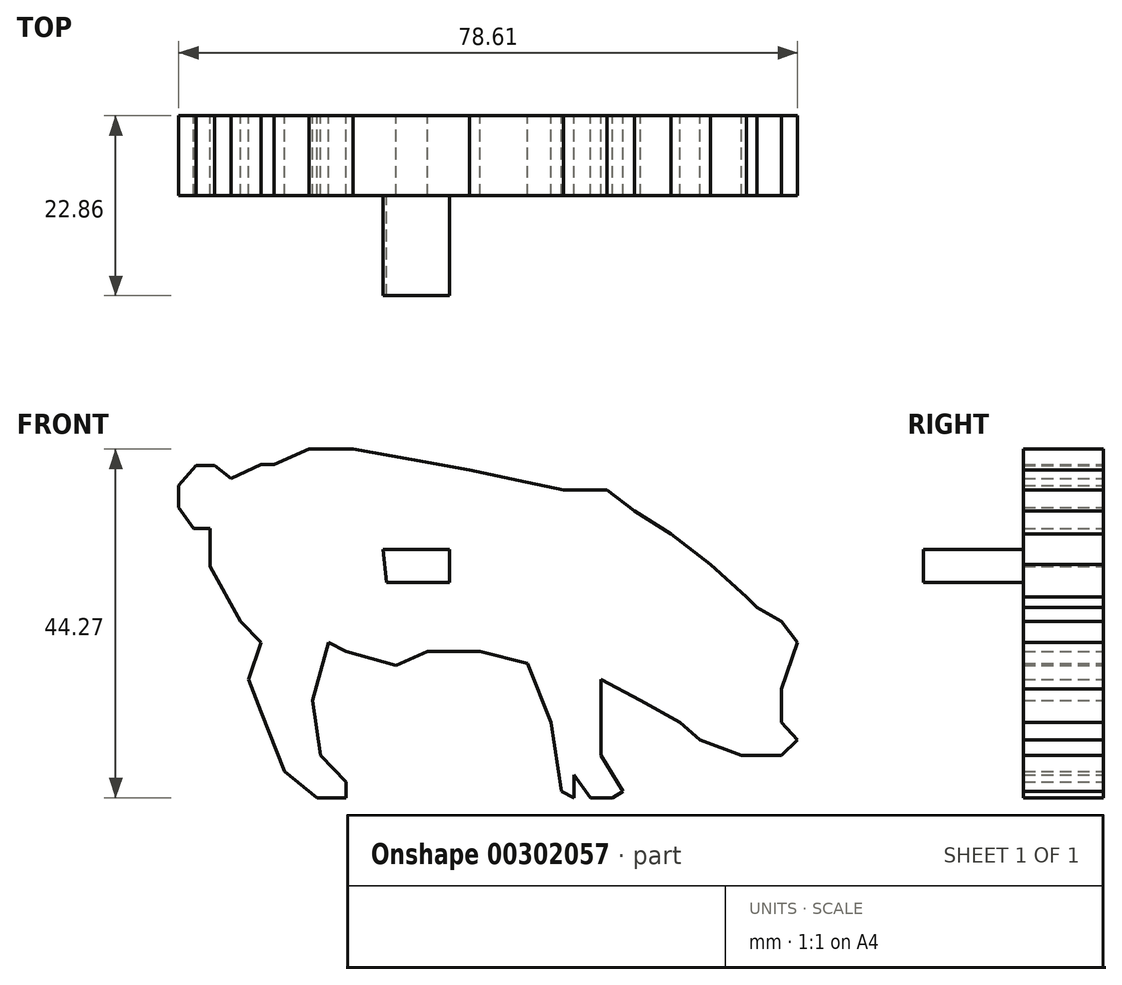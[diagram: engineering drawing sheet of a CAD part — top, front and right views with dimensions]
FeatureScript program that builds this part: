
annotation { "Feature Type Name" : "Feature", "Feature Type Description" : "" }
export const myFeature = defineFeature(function(context is Context, id is Id, definition is map)
    precondition{}
    {
        {
            var Q0;
            Q0=qCreatedBy(makeId("Front.planeOp"),FACE);
            var sketch = newSketch(context, id + "F0", { "sketchPlane" : qUnion([Q0])});
            skLineSegment(sketch, "E0", {"start": v(-64.38, 63.8) * mm, "end": v(-59.95, 65.71) * mm});
            skLineSegment(sketch, "E1", {"start": v(-59.95, 65.71) * mm, "end": v(-54.34, 65.71) * mm});
            skLineSegment(sketch, "E2", {"start": v(-54.34, 65.71) * mm, "end": v(-46.95, 64.38) * mm});
            skLineSegment(sketch, "E3", {"start": v(-46.95, 64.38) * mm, "end": v(-39.56, 63.05) * mm});
            skLineSegment(sketch, "E4", {"start": v(-39.56, 63.05) * mm, "end": v(-33.36, 61.72) * mm});
            skLineSegment(sketch, "E5", {"start": v(-33.36, 61.72) * mm, "end": v(-27.6, 60.54) * mm});
            skLineSegment(sketch, "E6", {"start": v(-27.6, 60.54) * mm, "end": v(-24.93, 60.54) * mm});
            skLineSegment(sketch, "E7", {"start": v(-24.93, 60.54) * mm, "end": v(-22.13, 60.54) * mm});
            skLineSegment(sketch, "E8", {"start": v(-22.13, 60.54) * mm, "end": v(-18.58, 57.88) * mm});
            skLineSegment(sketch, "E9", {"start": v(-18.58, 57.88) * mm, "end": v(-14, 54.93) * mm});
            skLineSegment(sketch, "E10", {"start": v(-14, 54.93) * mm, "end": v(-8.98, 51.09) * mm});
            skLineSegment(sketch, "E11", {"start": v(-8.98, 51.09) * mm, "end": v(-4.4, 46.95) * mm});
            skLineSegment(sketch, "E12", {"start": v(-4.4, 46.95) * mm, "end": v(-3.07, 45.62) * mm});
            skLineSegment(sketch, "E13", {"start": v(-3.07, 45.62) * mm, "end": v(0.04, 43.85) * mm});
            skLineSegment(sketch, "E14", {"start": v(0.04, 43.85) * mm, "end": v(2.1, 41.19) * mm});
            skLineSegment(sketch, "E15", {"start": v(2.1, 41.19) * mm, "end": v(0.04, 35.28) * mm});
            skLineSegment(sketch, "E16", {"start": v(0.04, 35.28) * mm, "end": v(0.04, 31) * mm});
            skLineSegment(sketch, "E17", {"start": v(0.04, 31) * mm, "end": v(2.1, 28.77) * mm});
            skLineSegment(sketch, "E18", {"start": v(2.1, 28.77) * mm, "end": v(0.04, 26.84) * mm});
            skLineSegment(sketch, "E19", {"start": v(0.04, 26.84) * mm, "end": v(-2.77, 26.84) * mm});
            skLineSegment(sketch, "E20", {"start": v(-2.77, 26.84) * mm, "end": v(-4.99, 26.84) * mm});
            skLineSegment(sketch, "E21", {"start": v(-4.99, 26.84) * mm, "end": v(-10.3, 28.77) * mm});
            skLineSegment(sketch, "E22", {"start": v(-10.3, 28.77) * mm, "end": v(-12.82, 31) * mm});
            skLineSegment(sketch, "E23", {"start": v(-12.82, 31) * mm, "end": v(-17.84, 33.8) * mm});
            skLineSegment(sketch, "E24", {"start": v(-17.84, 33.8) * mm, "end": v(-22.86, 36.46) * mm});
            skLineSegment(sketch, "E25", {"start": v(-22.86, 36.46) * mm, "end": v(-22.86, 31) * mm});
            skLineSegment(sketch, "E26", {"start": v(-22.86, 31) * mm, "end": v(-22.86, 26.84) * mm});
            skLineSegment(sketch, "E27", {"start": v(-22.86, 26.84) * mm, "end": v(-20.06, 22.27) * mm});
            skLineSegment(sketch, "E28", {"start": v(-20.06, 22.27) * mm, "end": v(-21.42, 21.44) * mm});
            skLineSegment(sketch, "E29", {"start": v(-21.42, 21.44) * mm, "end": v(-24.2, 21.44) * mm});
            skLineSegment(sketch, "E30", {"start": v(-24.2, 21.44) * mm, "end": v(-26.26, 24.34) * mm});
            skLineSegment(sketch, "E31", {"start": v(-26.26, 24.34) * mm, "end": v(-26.26, 21.44) * mm});
            skLineSegment(sketch, "E32", {"start": v(-26.26, 21.44) * mm, "end": v(-27.89, 22.27) * mm});
            skLineSegment(sketch, "E33", {"start": v(-27.89, 22.27) * mm, "end": v(-29.22, 31) * mm});
            skLineSegment(sketch, "E34", {"start": v(-29.22, 31) * mm, "end": v(-32.17, 38.53) * mm});
            skLineSegment(sketch, "E35", {"start": v(-32.17, 38.53) * mm, "end": v(-38.23, 40) * mm});
            skLineSegment(sketch, "E36", {"start": v(-38.23, 40) * mm, "end": v(-44.88, 40) * mm});
            skLineSegment(sketch, "E37", {"start": v(-44.88, 40) * mm, "end": v(-48.87, 38.23) * mm});
            skLineSegment(sketch, "E38", {"start": v(-48.87, 38.23) * mm, "end": v(-55.22, 40) * mm});
            skLineSegment(sketch, "E39", {"start": v(-55.22, 40) * mm, "end": v(-57.44, 41.19) * mm});
            skLineSegment(sketch, "E40", {"start": v(-57.44, 41.19) * mm, "end": v(-59.5, 33.8) * mm});
            skLineSegment(sketch, "E41", {"start": v(-59.5, 33.8) * mm, "end": v(-58.47, 26.84) * mm});
            skLineSegment(sketch, "E42", {"start": v(-58.47, 26.84) * mm, "end": v(-55.22, 23.46) * mm});
            skLineSegment(sketch, "E43", {"start": v(-55.22, 23.46) * mm, "end": v(-55.22, 21.44) * mm});
            skLineSegment(sketch, "E44", {"start": v(-55.22, 21.44) * mm, "end": v(-58.92, 21.44) * mm});
            skLineSegment(sketch, "E45", {"start": v(-58.92, 21.44) * mm, "end": v(-63.05, 24.79) * mm});
            skLineSegment(sketch, "E46", {"start": v(-63.05, 24.79) * mm, "end": v(-66, 32.32) * mm});
            skLineSegment(sketch, "E47", {"start": v(-66, 32.32) * mm, "end": v(-67.63, 36.46) * mm});
            skLineSegment(sketch, "E48", {"start": v(-67.63, 36.46) * mm, "end": v(-66, 41.19) * mm});
            skLineSegment(sketch, "E49", {"start": v(-66, 41.19) * mm, "end": v(-68.67, 43.85) * mm});
            skLineSegment(sketch, "E50", {"start": v(-68.67, 43.85) * mm, "end": v(-72.51, 50.8) * mm});
            skLineSegment(sketch, "E51", {"start": v(-72.51, 50.8) * mm, "end": v(-72.51, 55.67) * mm});
            skLineSegment(sketch, "E52", {"start": v(-72.51, 55.67) * mm, "end": v(-74.58, 55.67) * mm});
            skLineSegment(sketch, "E53", {"start": v(-74.58, 55.67) * mm, "end": v(-76.5, 58.33) * mm});
            skLineSegment(sketch, "E54", {"start": v(-76.5, 58.33) * mm, "end": v(-76.5, 61.13) * mm});
            skLineSegment(sketch, "E55", {"start": v(-76.5, 61.13) * mm, "end": v(-74.28, 63.65) * mm});
            skLineSegment(sketch, "E56", {"start": v(-74.28, 63.65) * mm, "end": v(-71.92, 63.65) * mm});
            skLineSegment(sketch, "E57", {"start": v(-71.92, 63.65) * mm, "end": v(-69.85, 62.02) * mm});
            skLineSegment(sketch, "E58", {"start": v(-69.85, 62.02) * mm, "end": v(-66, 63.8) * mm});
            skLineSegment(sketch, "E59", {"start": v(-66, 63.8) * mm, "end": v(-64.38, 63.8) * mm});
            skSolve(sketch);
        }
        {
            var Q0;
            Q0=makeQuery(id+"F0.imprint","IMPRINT",FACE,{"disambiguationData":[TD([[makeQuery(id+"F0.imprint","IMPRINT",EDGE,{"derivedFrom":sQuery(id+"F0.wireOp",EDGE,"E0")}),-1.0]])]});
            var Q1;
            Q1 = qConstructionFilter(qBodyType(qCreatedBy(id + "F0" ,EDGE), BodyType.WIRE), ConstructionObject.NO);
            extrude(context, id + "F1", {"entities" : qUnion([Q0]), "surfaceEntities" : qUnion([Q1]), "depth" : 10.16 * mm});
        }
        {
            var Q0;
            Q0=makeQuery(id+"F1.opExtrude","CAP_FACE",FACE,{"disambiguationData":[OSD([sQuery(id+"F0.wireOp",EDGE,"E0"),sQuery(id+"F0.wireOp",EDGE,"E1"),sQuery(id+"F0.wireOp",EDGE,"E2"),sQuery(id+"F0.wireOp",EDGE,"E3"),sQuery(id+"F0.wireOp",EDGE,"E4"),sQuery(id+"F0.wireOp",EDGE,"E5"),sQuery(id+"F0.wireOp",EDGE,"E6"),sQuery(id+"F0.wireOp",EDGE,"E7"),sQuery(id+"F0.wireOp",EDGE,"E8"),sQuery(id+"F0.wireOp",EDGE,"E9"),sQuery(id+"F0.wireOp",EDGE,"E10"),sQuery(id+"F0.wireOp",EDGE,"E11"),sQuery(id+"F0.wireOp",EDGE,"E12"),sQuery(id+"F0.wireOp",EDGE,"E13"),sQuery(id+"F0.wireOp",EDGE,"E14"),sQuery(id+"F0.wireOp",EDGE,"E15"),sQuery(id+"F0.wireOp",EDGE,"E16"),sQuery(id+"F0.wireOp",EDGE,"E17"),sQuery(id+"F0.wireOp",EDGE,"E18"),sQuery(id+"F0.wireOp",EDGE,"E19"),sQuery(id+"F0.wireOp",EDGE,"E20"),sQuery(id+"F0.wireOp",EDGE,"E21"),sQuery(id+"F0.wireOp",EDGE,"E22"),sQuery(id+"F0.wireOp",EDGE,"E23"),sQuery(id+"F0.wireOp",EDGE,"E24"),sQuery(id+"F0.wireOp",EDGE,"E25"),sQuery(id+"F0.wireOp",EDGE,"E26"),sQuery(id+"F0.wireOp",EDGE,"E27"),sQuery(id+"F0.wireOp",EDGE,"E28"),sQuery(id+"F0.wireOp",EDGE,"E29"),sQuery(id+"F0.wireOp",EDGE,"E30"),sQuery(id+"F0.wireOp",EDGE,"E31"),sQuery(id+"F0.wireOp",EDGE,"E32"),sQuery(id+"F0.wireOp",EDGE,"E33"),sQuery(id+"F0.wireOp",EDGE,"E34"),sQuery(id+"F0.wireOp",EDGE,"E35"),sQuery(id+"F0.wireOp",EDGE,"E36"),sQuery(id+"F0.wireOp",EDGE,"E37"),sQuery(id+"F0.wireOp",EDGE,"E38"),sQuery(id+"F0.wireOp",EDGE,"E39"),sQuery(id+"F0.wireOp",EDGE,"E40"),sQuery(id+"F0.wireOp",EDGE,"E41"),sQuery(id+"F0.wireOp",EDGE,"E42"),sQuery(id+"F0.wireOp",EDGE,"E43"),sQuery(id+"F0.wireOp",EDGE,"E44"),sQuery(id+"F0.wireOp",EDGE,"E45"),sQuery(id+"F0.wireOp",EDGE,"E46"),sQuery(id+"F0.wireOp",EDGE,"E47"),sQuery(id+"F0.wireOp",EDGE,"E48"),sQuery(id+"F0.wireOp",EDGE,"E49"),sQuery(id+"F0.wireOp",EDGE,"E50"),sQuery(id+"F0.wireOp",EDGE,"E51"),sQuery(id+"F0.wireOp",EDGE,"E52"),sQuery(id+"F0.wireOp",EDGE,"E53"),sQuery(id+"F0.wireOp",EDGE,"E54"),sQuery(id+"F0.wireOp",EDGE,"E55"),sQuery(id+"F0.wireOp",EDGE,"E56"),sQuery(id+"F0.wireOp",EDGE,"E57"),sQuery(id+"F0.wireOp",EDGE,"E58"),sQuery(id+"F0.wireOp",EDGE,"E59")])],"isStart":false});
            var sketch = newSketch(context, id + "F2", { "sketchPlane" : qUnion([Q0])});
            skLineSegment(sketch, "E60", {"start": v(-50.53, 52.97) * mm, "end": v(-42.11, 52.97) * mm});
            skLineSegment(sketch, "E61", {"start": v(-42.11, 52.97) * mm, "end": v(-42.11, 48.76) * mm});
            skLineSegment(sketch, "E62", {"start": v(-42.11, 48.76) * mm, "end": v(-50.09, 48.76) * mm});
            skLineSegment(sketch, "E63", {"start": v(-50.09, 48.76) * mm, "end": v(-50.53, 52.97) * mm});
            skSolve(sketch);
        }
        {
            var Q0;
            Q0 = qSketchRegion(id + "F2", true);
            extrude(context, id + "F3", {"entities" : qUnion([Q0]), "operationType" : NewBodyOperationType.ADD, "depth" : 12.7 * mm});
        }
    });
